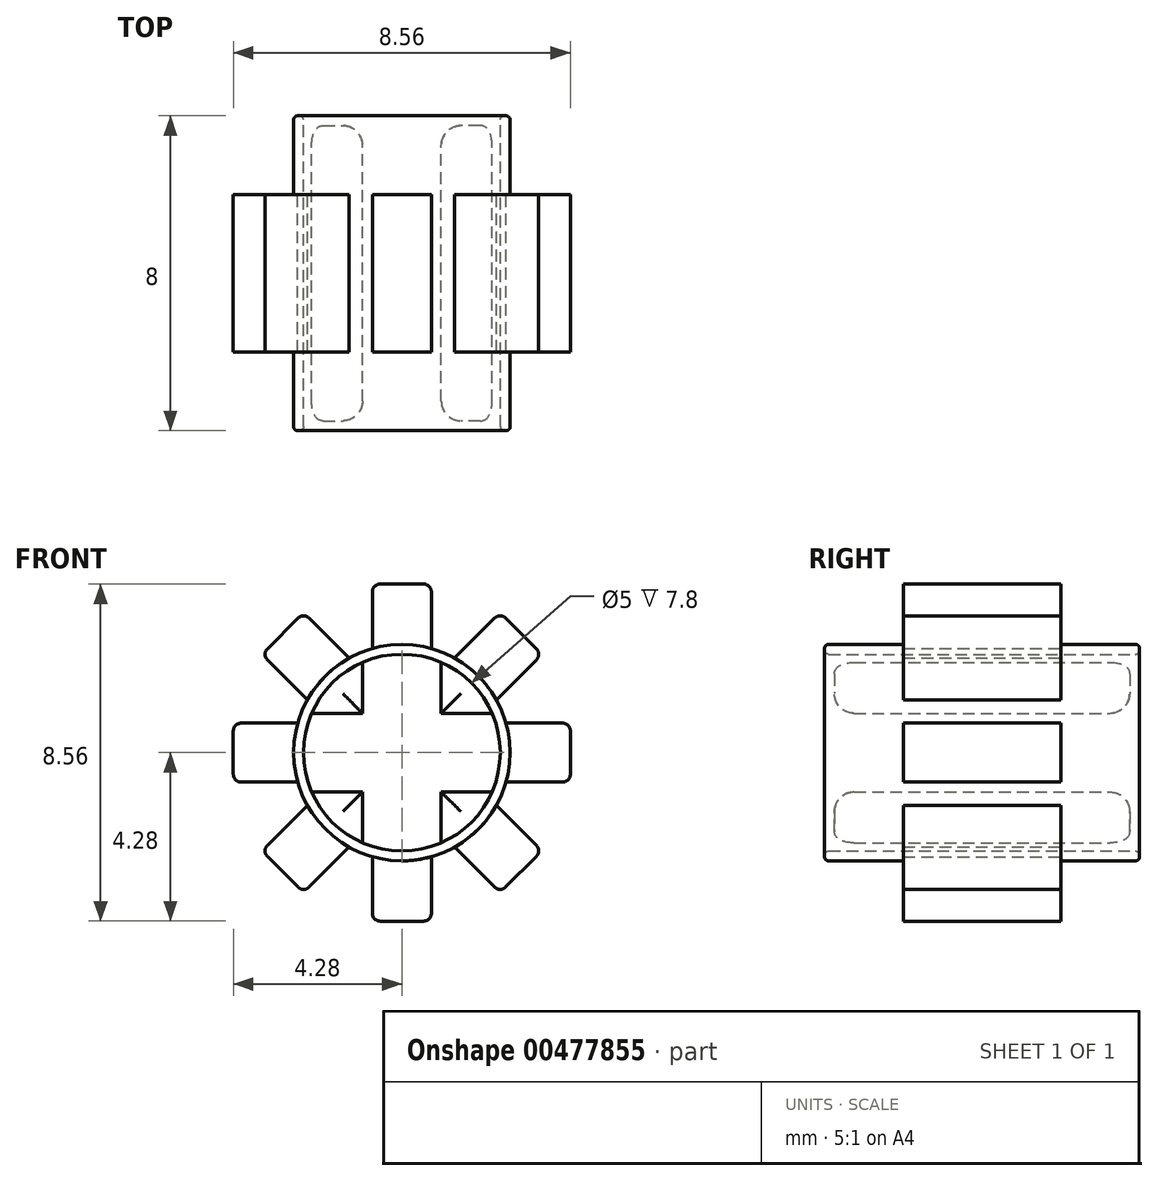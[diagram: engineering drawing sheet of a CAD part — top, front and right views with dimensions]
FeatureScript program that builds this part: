
annotation { "Feature Type Name" : "Feature", "Feature Type Description" : "" }
export const myFeature = defineFeature(function(context is Context, id is Id, definition is map)
    precondition{}
    {
        {
            var Q0;
            Q0=qCreatedBy(makeId("Front.planeOp"),FACE);
            var sketch = newSketch(context, id + "F0", { "sketchPlane" : qUnion([Q0])});
            skCircle(sketch, "E0", {"center": v(0, 0) * mm, "radius": 2.75 * mm});
            skCircle(sketch, "E1", {"center": v(0, 0) * mm, "radius": 2.5 * mm});
            skLineSegment(sketch, "E2", {"start": v(0, 4.28) * mm, "end": v(0.55, 4.28) * mm});
            skLineSegment(sketch, "E3", {"start": v(0.75, 4.08) * mm, "end": v(0.75, 2.65) * mm});
            skLineSegment(sketch, "E4", {"start": v(0, 4.28) * mm, "end": v(-0.55, 4.28) * mm});
            skLineSegment(sketch, "E5", {"start": v(-0.75, 4.08) * mm, "end": v(-0.75, 2.65) * mm});
            skPoint(sketch, "E6.visualSharp", {"position": v(-0.75, 4.28) * mm});
            skArc(sketch, "E6.filletArc", {"start": v(-0.55, 4.28) * mm, "mid": v(-0.7, 4.22) * mm, "end": v(-0.75, 4.08) * mm});
            skPoint(sketch, "E7.visualSharp", {"position": v(0.75, 4.28) * mm});
            skArc(sketch, "E7.filletArc", {"start": v(0.75, 4.08) * mm, "mid": v(0.7, 4.22) * mm, "end": v(0.55, 4.28) * mm});
            skLineSegment(sketch, "E8.1.0", {"start": v(-3.42, 2.36) * mm, "end": v(-2.4, 1.34) * mm});
            skLineSegment(sketch, "E8.1.1", {"start": v(-2.36, 3.42) * mm, "end": v(-1.34, 2.4) * mm});
            skArc(sketch, "E8.1.2", {"start": v(-2.36, 3.42) * mm, "mid": v(-2.5, 3.48) * mm, "end": v(-2.64, 3.42) * mm});
            skArc(sketch, "E8.1.3", {"start": v(-3.42, 2.64) * mm, "mid": v(-3.48, 2.5) * mm, "end": v(-3.42, 2.36) * mm});
            skLineSegment(sketch, "E8.1.4", {"start": v(-3.03, 3.03) * mm, "end": v(-3.42, 2.64) * mm});
            skLineSegment(sketch, "E8.1.5", {"start": v(-3.03, 3.03) * mm, "end": v(-2.64, 3.42) * mm});
            skLineSegment(sketch, "E8.2.0", {"start": v(-4.08, -0.75) * mm, "end": v(-2.65, -0.75) * mm});
            skLineSegment(sketch, "E8.2.1", {"start": v(-4.08, 0.75) * mm, "end": v(-2.65, 0.75) * mm});
            skArc(sketch, "E8.2.2", {"start": v(-4.08, 0.75) * mm, "mid": v(-4.22, 0.7) * mm, "end": v(-4.28, 0.55) * mm});
            skArc(sketch, "E8.2.3", {"start": v(-4.28, -0.55) * mm, "mid": v(-4.22, -0.7) * mm, "end": v(-4.08, -0.75) * mm});
            skLineSegment(sketch, "E8.2.4", {"start": v(-4.28, 0) * mm, "end": v(-4.28, -0.55) * mm});
            skLineSegment(sketch, "E8.2.5", {"start": v(-4.28, 0) * mm, "end": v(-4.28, 0.55) * mm});
            skLineSegment(sketch, "E8.3.0", {"start": v(-2.36, -3.42) * mm, "end": v(-1.34, -2.4) * mm});
            skLineSegment(sketch, "E8.3.1", {"start": v(-3.42, -2.36) * mm, "end": v(-2.4, -1.34) * mm});
            skArc(sketch, "E8.3.2", {"start": v(-3.42, -2.36) * mm, "mid": v(-3.48, -2.5) * mm, "end": v(-3.42, -2.64) * mm});
            skArc(sketch, "E8.3.3", {"start": v(-2.64, -3.42) * mm, "mid": v(-2.5, -3.48) * mm, "end": v(-2.36, -3.42) * mm});
            skLineSegment(sketch, "E8.3.4", {"start": v(-3.03, -3.03) * mm, "end": v(-2.64, -3.42) * mm});
            skLineSegment(sketch, "E8.3.5", {"start": v(-3.03, -3.03) * mm, "end": v(-3.42, -2.64) * mm});
            skLineSegment(sketch, "E8.4.0", {"start": v(0.75, -4.08) * mm, "end": v(0.75, -2.65) * mm});
            skLineSegment(sketch, "E8.4.1", {"start": v(-0.75, -4.08) * mm, "end": v(-0.75, -2.65) * mm});
            skArc(sketch, "E8.4.2", {"start": v(-0.75, -4.08) * mm, "mid": v(-0.7, -4.22) * mm, "end": v(-0.55, -4.28) * mm});
            skArc(sketch, "E8.4.3", {"start": v(0.55, -4.28) * mm, "mid": v(0.7, -4.22) * mm, "end": v(0.75, -4.08) * mm});
            skLineSegment(sketch, "E8.4.4", {"start": v(0, -4.28) * mm, "end": v(0.55, -4.28) * mm});
            skLineSegment(sketch, "E8.4.5", {"start": v(0, -4.28) * mm, "end": v(-0.55, -4.28) * mm});
            skLineSegment(sketch, "E8.5.0", {"start": v(3.42, -2.36) * mm, "end": v(2.4, -1.34) * mm});
            skLineSegment(sketch, "E8.5.1", {"start": v(2.36, -3.42) * mm, "end": v(1.34, -2.4) * mm});
            skArc(sketch, "E8.5.2", {"start": v(2.36, -3.42) * mm, "mid": v(2.5, -3.48) * mm, "end": v(2.64, -3.42) * mm});
            skArc(sketch, "E8.5.3", {"start": v(3.42, -2.64) * mm, "mid": v(3.48, -2.5) * mm, "end": v(3.42, -2.36) * mm});
            skLineSegment(sketch, "E8.5.4", {"start": v(3.03, -3.03) * mm, "end": v(3.42, -2.64) * mm});
            skLineSegment(sketch, "E8.5.5", {"start": v(3.03, -3.03) * mm, "end": v(2.64, -3.42) * mm});
            skLineSegment(sketch, "E8.6.0", {"start": v(4.08, 0.75) * mm, "end": v(2.65, 0.75) * mm});
            skLineSegment(sketch, "E8.6.1", {"start": v(4.08, -0.75) * mm, "end": v(2.65, -0.75) * mm});
            skArc(sketch, "E8.6.2", {"start": v(4.08, -0.75) * mm, "mid": v(4.22, -0.7) * mm, "end": v(4.28, -0.55) * mm});
            skArc(sketch, "E8.6.3", {"start": v(4.28, 0.55) * mm, "mid": v(4.22, 0.7) * mm, "end": v(4.08, 0.75) * mm});
            skLineSegment(sketch, "E8.6.4", {"start": v(4.28, 0) * mm, "end": v(4.28, 0.55) * mm});
            skLineSegment(sketch, "E8.6.5", {"start": v(4.28, 0) * mm, "end": v(4.28, -0.55) * mm});
            skLineSegment(sketch, "E8.7.0", {"start": v(2.36, 3.42) * mm, "end": v(1.34, 2.4) * mm});
            skLineSegment(sketch, "E8.7.1", {"start": v(3.42, 2.36) * mm, "end": v(2.4, 1.34) * mm});
            skArc(sketch, "E8.7.2", {"start": v(3.42, 2.36) * mm, "mid": v(3.48, 2.5) * mm, "end": v(3.42, 2.64) * mm});
            skArc(sketch, "E8.7.3", {"start": v(2.64, 3.42) * mm, "mid": v(2.5, 3.48) * mm, "end": v(2.36, 3.42) * mm});
            skLineSegment(sketch, "E8.7.4", {"start": v(3.03, 3.03) * mm, "end": v(2.64, 3.42) * mm});
            skLineSegment(sketch, "E8.7.5", {"start": v(3.03, 3.03) * mm, "end": v(3.42, 2.64) * mm});
            skPoint(sketch, "E9.endSnap0", {"position": v(0, 1.25) * mm});
            skLineSegment(sketch, "E10", {"start": v(2.3, -1) * mm, "end": v(1, -1) * mm});
            skLineSegment(sketch, "E11", {"start": v(1, -2.3) * mm, "end": v(1, -1) * mm});
            skLineSegment(sketch, "E12.MirrorCS", {"start": v(-1, -2.3) * mm, "end": v(-1, -1) * mm});
            skLineSegment(sketch, "E13.MirrorCS", {"start": v(-2.3, -1) * mm, "end": v(-1, -1) * mm});
            skLineSegment(sketch, "E14.MirrorCS", {"start": v(-1, 2.3) * mm, "end": v(-1, 1) * mm});
            skLineSegment(sketch, "E15.MirrorCS", {"start": v(-2.3, 1) * mm, "end": v(-1, 1) * mm});
            skLineSegment(sketch, "E16.MirrorCS", {"start": v(1, 2.3) * mm, "end": v(1, 1) * mm});
            skLineSegment(sketch, "E17.MirrorCS", {"start": v(2.3, 1) * mm, "end": v(1, 1) * mm});
            skSolve(sketch);
        }
        {
            var Q0;
            {var subQ14=sQuery(id+"F0.wireOp",EDGE,"E0");var subQ15=makeQuery(id+"F0.imprint","INTERSECT",VERTEX,{"derivedFrom":[subQ14,sQuery(id+"F0.wireOp",EDGE,"E8.6.0")]});Q0=makeQuery(id+"F0.imprint","IMPRINT",FACE,{"disambiguationData":[TD([[makeQuery(id+"F0.imprint","IMPRINT",EDGE,{"disambiguationData":[TD([[subQ15,-1.0]])],"derivedFrom":subQ14}),1.0]])]});}
            extrude(context, id + "F1", {"entities" : qUnion([Q0]), "endBound" : BoundingType.SYMMETRIC, "depth" : 8 * mm, "offsetDistance" : 25 * mm});
        }
        {
            var Q0;
            Q0=makeQuery(id+"F0.imprint","IMPRINT",FACE,{"disambiguationData":[TD([[makeQuery(id+"F0.imprint","IMPRINT",EDGE,{"derivedFrom":sQuery(id+"F0.wireOp",EDGE,"E2")}),-1.0]])]});
            var Q1;
            {var subQ0=sQuery(id+"F0.wireOp",EDGE,"E8.7.0");Q1=makeQuery(id+"F0.imprint","IMPRINT",FACE,{"disambiguationData":[TD([[makeQuery(id+"F0.imprint","IMPRINT",EDGE,{"derivedFrom":subQ0}),1.0]])]});}
            var Q2;
            {var subQ0=sQuery(id+"F0.wireOp",EDGE,"E8.6.0");Q2=makeQuery(id+"F0.imprint","IMPRINT",FACE,{"disambiguationData":[TD([[makeQuery(id+"F0.imprint","IMPRINT",EDGE,{"derivedFrom":subQ0}),1.0]])]});}
            var Q3;
            {var subQ1=sQuery(id+"F0.wireOp",EDGE,"E8.5.0");Q3=makeQuery(id+"F0.imprint","IMPRINT",FACE,{"disambiguationData":[TD([[makeQuery(id+"F0.imprint","IMPRINT",EDGE,{"derivedFrom":subQ1}),1.0]])]});}
            var Q4;
            {var subQ1=sQuery(id+"F0.wireOp",EDGE,"E8.4.0");Q4=makeQuery(id+"F0.imprint","IMPRINT",FACE,{"disambiguationData":[TD([[makeQuery(id+"F0.imprint","IMPRINT",EDGE,{"derivedFrom":subQ1}),1.0]])]});}
            var Q5;
            {var subQ1=sQuery(id+"F0.wireOp",EDGE,"E8.3.0");Q5=makeQuery(id+"F0.imprint","IMPRINT",FACE,{"disambiguationData":[TD([[makeQuery(id+"F0.imprint","IMPRINT",EDGE,{"derivedFrom":subQ1}),1.0]])]});}
            var Q6;
            {var subQ1=sQuery(id+"F0.wireOp",EDGE,"E8.2.0");Q6=makeQuery(id+"F0.imprint","IMPRINT",FACE,{"disambiguationData":[TD([[makeQuery(id+"F0.imprint","IMPRINT",EDGE,{"derivedFrom":subQ1}),1.0]])]});}
            var Q7;
            {var subQ0=sQuery(id+"F0.wireOp",EDGE,"E8.1.0");Q7=makeQuery(id+"F0.imprint","IMPRINT",FACE,{"disambiguationData":[TD([[makeQuery(id+"F0.imprint","IMPRINT",EDGE,{"derivedFrom":subQ0}),1.0]])]});}
            extrude(context, id + "F2", {"entities" : qUnion([Q0, Q1, Q2, Q3, Q4, Q5, Q6, Q7]), "operationType" : NewBodyOperationType.ADD, "endBound" : BoundingType.SYMMETRIC, "depth" : 4 * mm, "offsetDistance" : 25 * mm});
        }
        {
            var Q0;
            Q0=makeQuery(id+"F1.opExtrude","CAP_EDGE",EDGE,{"disambiguationData":[OSD([sQuery(id+"F0.wireOp",EDGE,"E0")])],"isStart":false});
            var Q1;
            Q1=makeQuery(id+"F1.opExtrude","CAP_EDGE",EDGE,{"disambiguationData":[OSD([sQuery(id+"F0.wireOp",EDGE,"E1")])],"isStart":false});
            var Q2;
            Q2=makeQuery(id+"F1.opExtrude","CAP_EDGE",EDGE,{"disambiguationData":[OSD([sQuery(id+"F0.wireOp",EDGE,"E0")])],"isStart":true});
            var Q3;
            Q3=makeQuery(id+"F1.opExtrude","CAP_EDGE",EDGE,{"disambiguationData":[OSD([sQuery(id+"F0.wireOp",EDGE,"E1")])],"isStart":true});
            fillet(context, id + "F3", {"entities" : qUnion([Q0, Q1, Q2, Q3]), "radius" : 0.1 * mm, "tangentPropagation" : true, "allowEdgeOverflow" : false});
        }
        {
            var Q0;
            {var subQ0=sQuery(id+"F0.wireOp",EDGE,"E14.MirrorCS");Q0=makeQuery(id+"F0.imprint","IMPRINT",FACE,{"disambiguationData":[TD([[makeQuery(id+"F0.imprint","IMPRINT",EDGE,{"derivedFrom":subQ0}),-1.0]])]});}
            var Q1;
            {var subQ0=sQuery(id+"F0.wireOp",EDGE,"E16.MirrorCS");Q1=makeQuery(id+"F0.imprint","IMPRINT",FACE,{"disambiguationData":[TD([[makeQuery(id+"F0.imprint","IMPRINT",EDGE,{"derivedFrom":subQ0}),1.0]])]});}
            var Q2;
            {var subQ0=sQuery(id+"F0.wireOp",EDGE,"E10");Q2=makeQuery(id+"F0.imprint","IMPRINT",FACE,{"disambiguationData":[TD([[makeQuery(id+"F0.imprint","IMPRINT",EDGE,{"derivedFrom":subQ0}),1.0]])]});}
            var Q3;
            {var subQ0=sQuery(id+"F0.wireOp",EDGE,"E12.MirrorCS");Q3=makeQuery(id+"F0.imprint","IMPRINT",FACE,{"disambiguationData":[TD([[makeQuery(id+"F0.imprint","IMPRINT",EDGE,{"derivedFrom":subQ0}),1.0]])]});}
            extrude(context, id + "F4", {"entities" : qUnion([Q0, Q1, Q2, Q3]), "operationType" : NewBodyOperationType.ADD, "endBound" : BoundingType.SYMMETRIC, "depth" : 7.5 * mm, "offsetDistance" : 25 * mm});
        }
        {
            var Q0;
            Q0=makeQuery(id+"F4.opExtrude","CAP_EDGE",EDGE,{"disambiguationData":[OSD([sQuery(id+"F0.wireOp",EDGE,"E14.MirrorCS")])],"isStart":false});
            var Q1;
            Q1=makeQuery(id+"F4.opExtrude","CAP_EDGE",EDGE,{"disambiguationData":[OSD([sQuery(id+"F0.wireOp",EDGE,"E15.MirrorCS")])],"isStart":false});
            var Q2;
            Q2=makeQuery(id+"F4.opExtrude","CAP_EDGE",EDGE,{"disambiguationData":[OSD([sQuery(id+"F0.wireOp",EDGE,"E13.MirrorCS")])],"isStart":false});
            var Q3;
            Q3=makeQuery(id+"F4.opExtrude","CAP_EDGE",EDGE,{"disambiguationData":[OSD([sQuery(id+"F0.wireOp",EDGE,"E12.MirrorCS")])],"isStart":false});
            var Q4;
            Q4=makeQuery(id+"F4.opExtrude","CAP_EDGE",EDGE,{"disambiguationData":[OSD([sQuery(id+"F0.wireOp",EDGE,"E16.MirrorCS")])],"isStart":false});
            var Q5;
            Q5=makeQuery(id+"F4.opExtrude","CAP_EDGE",EDGE,{"disambiguationData":[OSD([sQuery(id+"F0.wireOp",EDGE,"E17.MirrorCS")])],"isStart":false});
            var Q6;
            Q6=makeQuery(id+"F4.opExtrude","CAP_EDGE",EDGE,{"disambiguationData":[OSD([sQuery(id+"F0.wireOp",EDGE,"E10")])],"isStart":false});
            var Q7;
            Q7=makeQuery(id+"F4.opExtrude","CAP_EDGE",EDGE,{"disambiguationData":[OSD([sQuery(id+"F0.wireOp",EDGE,"E11")])],"isStart":false});
            var Q8;
            Q8=makeQuery(id+"F4.opExtrude","CAP_EDGE",EDGE,{"disambiguationData":[OSD([sQuery(id+"F0.wireOp",EDGE,"E17.MirrorCS")])],"isStart":true});
            var Q9;
            Q9=makeQuery(id+"F4.opExtrude","CAP_EDGE",EDGE,{"disambiguationData":[OSD([sQuery(id+"F0.wireOp",EDGE,"E16.MirrorCS")])],"isStart":true});
            var Q10;
            Q10=makeQuery(id+"F4.opExtrude","CAP_EDGE",EDGE,{"disambiguationData":[OSD([sQuery(id+"F0.wireOp",EDGE,"E14.MirrorCS")])],"isStart":true});
            var Q11;
            Q11=makeQuery(id+"F4.opExtrude","CAP_EDGE",EDGE,{"disambiguationData":[OSD([sQuery(id+"F0.wireOp",EDGE,"E15.MirrorCS")])],"isStart":true});
            var Q12;
            Q12=makeQuery(id+"F4.opExtrude","CAP_EDGE",EDGE,{"disambiguationData":[OSD([sQuery(id+"F0.wireOp",EDGE,"E13.MirrorCS")])],"isStart":true});
            var Q13;
            Q13=makeQuery(id+"F4.opExtrude","CAP_EDGE",EDGE,{"disambiguationData":[OSD([sQuery(id+"F0.wireOp",EDGE,"E12.MirrorCS")])],"isStart":true});
            var Q14;
            Q14=makeQuery(id+"F4.opExtrude","CAP_EDGE",EDGE,{"disambiguationData":[OSD([sQuery(id+"F0.wireOp",EDGE,"E11")])],"isStart":true});
            var Q15;
            Q15=makeQuery(id+"F4.opExtrude","CAP_EDGE",EDGE,{"disambiguationData":[OSD([sQuery(id+"F0.wireOp",EDGE,"E10")])],"isStart":true});
            fillet(context, id + "F5", {"entities" : qUnion([Q0, Q1, Q2, Q3, Q4, Q5, Q6, Q7, Q8, Q9, Q10, Q11, Q12, Q13, Q14, Q15]), "radius" : 0.5 * mm, "tangentPropagation" : true, "allowEdgeOverflow" : false});
        }
    });
